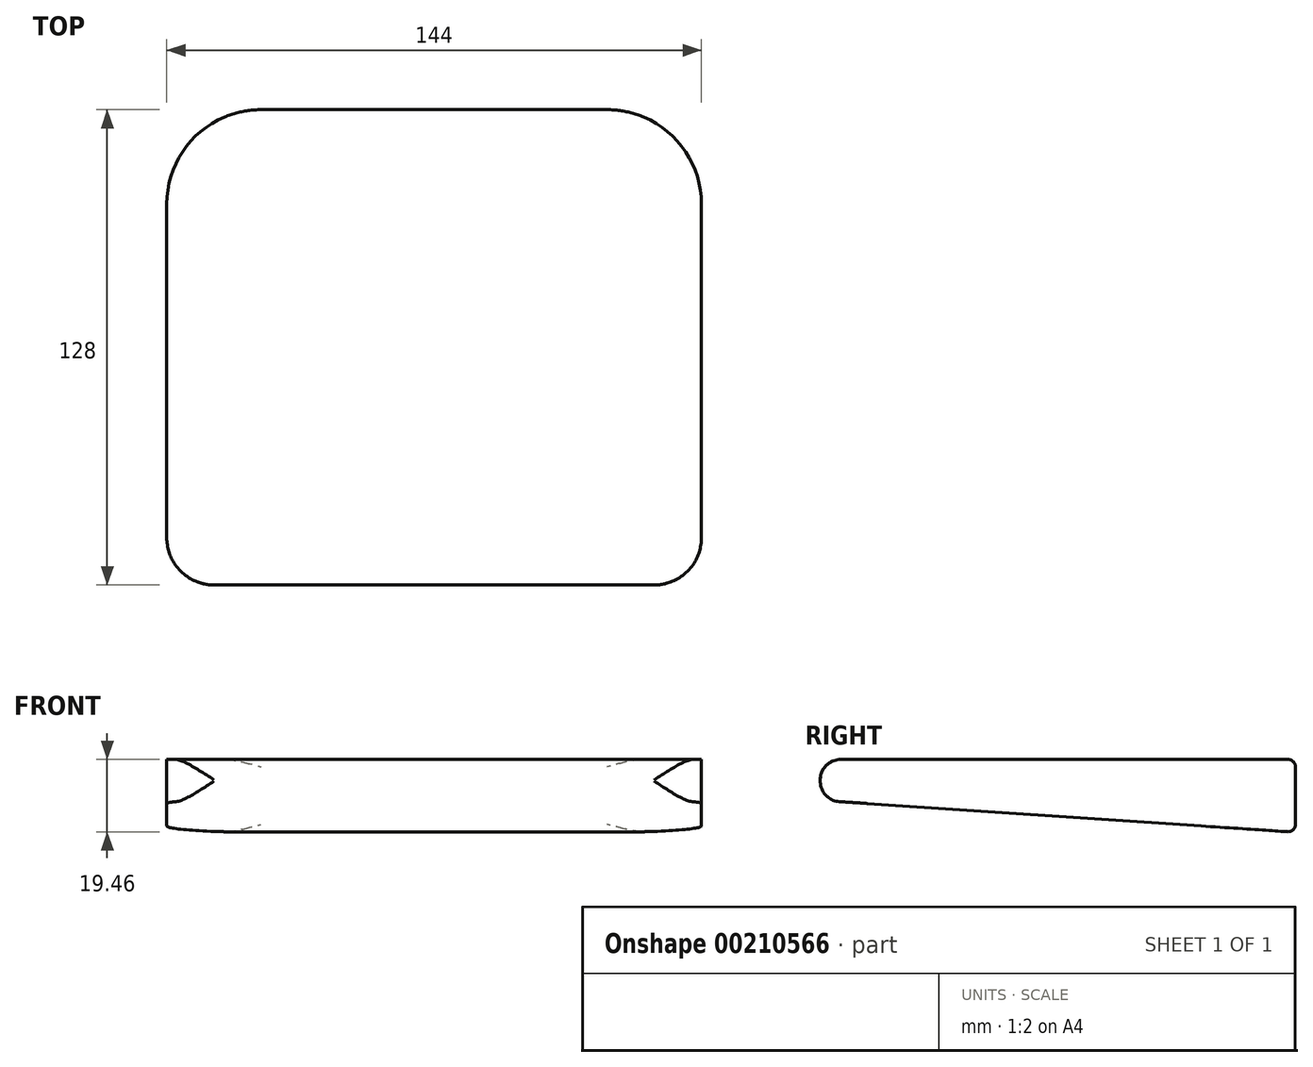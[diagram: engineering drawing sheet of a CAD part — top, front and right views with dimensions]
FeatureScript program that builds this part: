
annotation { "Feature Type Name" : "Feature", "Feature Type Description" : "" }
export const myFeature = defineFeature(function(context is Context, id is Id, definition is map)
    precondition{}
    {
        {
            var Q0;
            Q0=qCreatedBy(makeId("Right.planeOp"),FACE);
            var sketch = newSketch(context, id + "F0", { "sketchPlane" : qUnion([Q0])});
            skLineSegment(sketch, "E0", {"start": v(-2, 0) * mm, "end": v(-122.5, 0) * mm});
            skLineSegment(sketch, "E1", {"start": v(-128, -5.5) * mm, "end": v(-128, -5.86) * mm});
            skLineSegment(sketch, "E2", {"start": v(0, -2) * mm, "end": v(0, -17.46) * mm});
            skLineSegment(sketch, "E3", {"start": v(-2.13, -19.46) * mm, "end": v(-122.87, -11.34) * mm});
            skPoint(sketch, "E4.visualSharp", {"position": v(0, -19.6) * mm});
            skArc(sketch, "E4.filletArc", {"start": v(-2.13, -19.46) * mm, "mid": v(-0.63, -18.92) * mm, "end": v(0, -17.46) * mm});
            skPoint(sketch, "E5.visualSharp", {"position": v(0, 0) * mm});
            skArc(sketch, "E5.filletArc", {"start": v(0, -2) * mm, "mid": v(-0.59, -0.59) * mm, "end": v(-2, 0) * mm});
            skPoint(sketch, "E6.visualSharp", {"position": v(-128, -11) * mm});
            skArc(sketch, "E6.filletArc", {"start": v(-128, -5.86) * mm, "mid": v(-126.52, -9.61) * mm, "end": v(-122.87, -11.34) * mm});
            skPoint(sketch, "E7.visualSharp", {"position": v(-128, 0) * mm});
            skArc(sketch, "E7.filletArc", {"start": v(-122.5, 0) * mm, "mid": v(-126.39, -1.61) * mm, "end": v(-128, -5.5) * mm});
            skSolve(sketch);
        }
        {
            var Q0;
            Q0 = qSketchRegion(id + "F0", true);
            extrude(context, id + "F1", {"entities" : qUnion([Q0]), "oppositeDirection" : true, "depth" : 144 * mm});
        }
        {
            var Q0;
            Q0=makeQuery(id+"F1.opExtrude","SWEPT_FACE",FACE,{"disambiguationData":[OSD([sQuery(id+"F0.wireOp",EDGE,"E0")])]});
            var sketch = newSketch(context, id + "F2", { "sketchPlane" : qUnion([Q0])});
            skLineSegment(sketch, "E8", {"start": v(-144, -25.4) * mm, "end": v(-144, -115.3) * mm});
            skLineSegment(sketch, "E9", {"start": v(-131.3, -128) * mm, "end": v(-12.7, -128) * mm});
            skLineSegment(sketch, "E10", {"start": v(0, -115.3) * mm, "end": v(0, -25.4) * mm});
            skLineSegment(sketch, "E11", {"start": v(-25.4, 0) * mm, "end": v(-118.6, 0) * mm});
            skPoint(sketch, "E12.visualSharp", {"position": v(-144, 0) * mm});
            skArc(sketch, "E12.filletArc", {"start": v(-118.6, 0) * mm, "mid": v(-136.56, -7.44) * mm, "end": v(-144, -25.4) * mm});
            skPoint(sketch, "E13.visualSharp", {"position": v(0, 0) * mm});
            skArc(sketch, "E13.filletArc", {"start": v(0, -25.4) * mm, "mid": v(-7.44, -7.44) * mm, "end": v(-25.4, 0) * mm});
            skPoint(sketch, "E14.visualSharp", {"position": v(-144, -128) * mm});
            skArc(sketch, "E14.filletArc", {"start": v(-144, -115.3) * mm, "mid": v(-140.28, -124.28) * mm, "end": v(-131.3, -128) * mm});
            skPoint(sketch, "E15.visualSharp", {"position": v(0, -128) * mm});
            skArc(sketch, "E15.filletArc", {"start": v(-12.7, -128) * mm, "mid": v(-3.72, -124.28) * mm, "end": v(0, -115.3) * mm});
            skSolve(sketch);
        }
        {
            var Q0;
            Q0 = qSketchRegion(id + "F2", true);
            extrude(context, id + "F3", {"entities" : qUnion([Q0]), "operationType" : NewBodyOperationType.INTERSECT, "oppositeDirection" : true, "depth" : 25.4 * mm});
        }
    });
